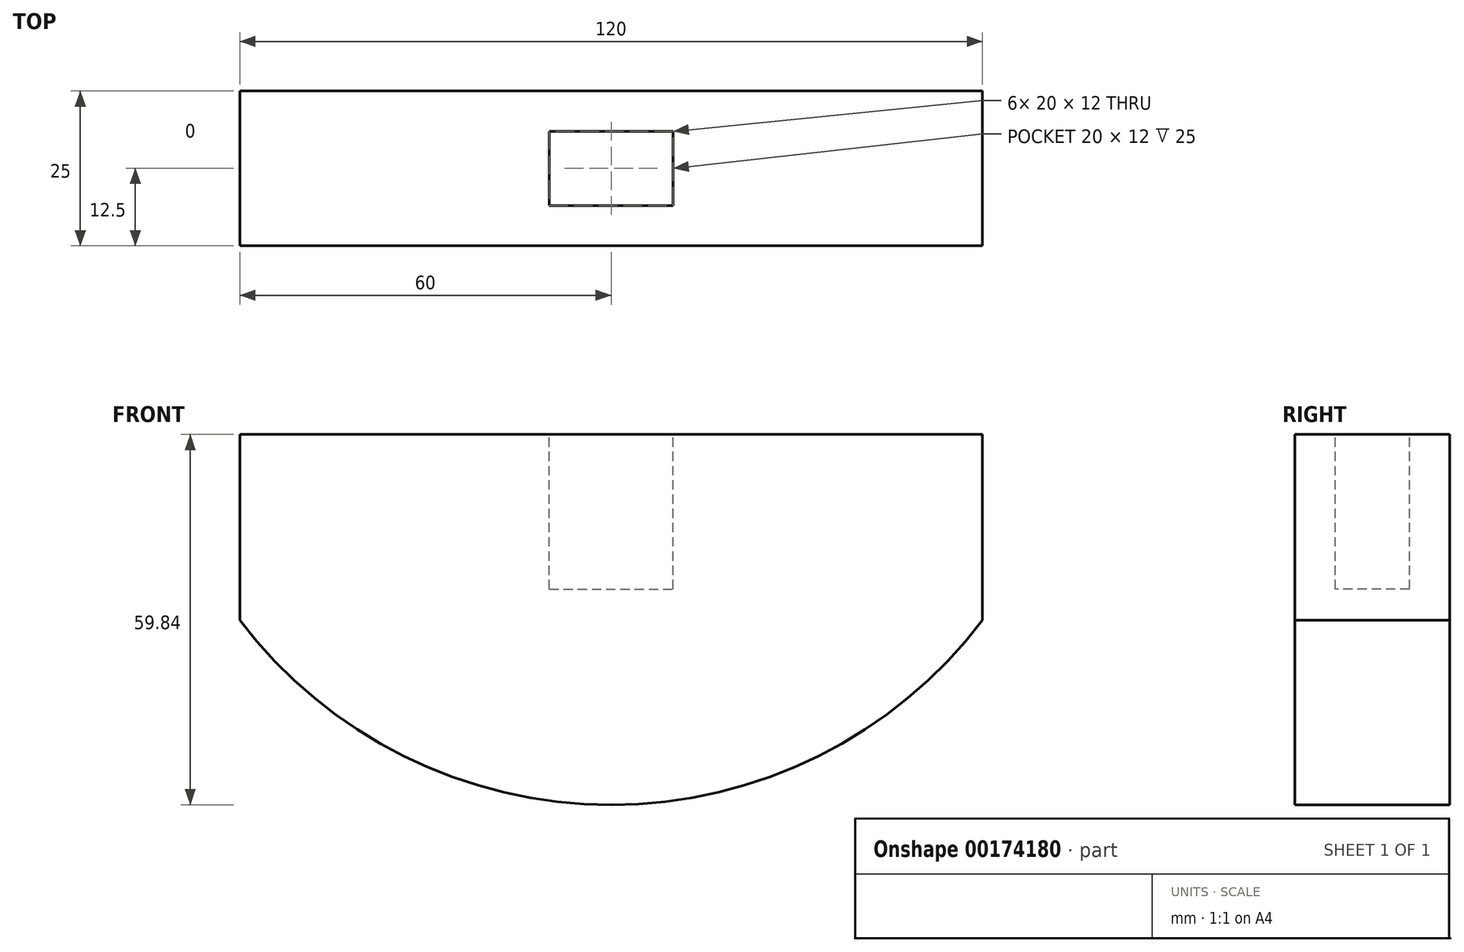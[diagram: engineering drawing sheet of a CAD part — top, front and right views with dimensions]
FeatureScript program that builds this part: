
annotation { "Feature Type Name" : "Feature", "Feature Type Description" : "" }
export const myFeature = defineFeature(function(context is Context, id is Id, definition is map)
    precondition{}
    {
        {
            var Q0;
            Q0=qCreatedBy(makeId("Front.planeOp"),FACE);
            var sketch = newSketch(context, id + "F0", { "sketchPlane" : qUnion([Q0])});
            skLineSegment(sketch, "E0.bottom", {"start": v(-60, 30) * mm, "end": v(60, 30) * mm});
            skLineSegment(sketch, "E0.left", {"start": v(-60, 30) * mm, "end": v(-60, 0) * mm});
            skLineSegment(sketch, "E0.right", {"start": v(60, 30) * mm, "end": v(60, 0) * mm});
            skArc(sketch, "E1", {"start": v(-60, 0) * mm, "mid": v(0, -29.84) * mm, "end": v(60, 0) * mm});
            skPoint(sketch, "E0.top.start.orphan", {"position": v(-60, -30) * mm});
            skPoint(sketch, "E2.orphan", {"position": v(60, -30) * mm});
            skSolve(sketch);
        }
        {
            var Q0;
            Q0=makeQuery(id+"F0.imprint","IMPRINT",FACE,{"disambiguationData":[TD([[makeQuery(id+"F0.imprint","IMPRINT",EDGE,{"derivedFrom":sQuery(id+"F0.wireOp",EDGE,"E0.bottom")}),-1.0]])]});
            extrude(context, id + "F1", {"entities" : qUnion([Q0]), "depth" : 25 * mm});
        }
        {
            var Q0;
            Q0=makeQuery(id+"F1.opExtrude","SWEPT_FACE",FACE,{"disambiguationData":[OSD([sQuery(id+"F0.wireOp",EDGE,"E0.bottom")])]});
            var sketch = newSketch(context, id + "F2", { "sketchPlane" : qUnion([Q0])});
            skLineSegment(sketch, "E3.bottom", {"start": v(-10, -6.5) * mm, "end": v(10, -6.5) * mm});
            skLineSegment(sketch, "E3.top", {"start": v(-10, -18.5) * mm, "end": v(10, -18.5) * mm});
            skLineSegment(sketch, "E3.left", {"start": v(-10, -6.5) * mm, "end": v(-10, -18.5) * mm});
            skLineSegment(sketch, "E3.right", {"start": v(10, -6.5) * mm, "end": v(10, -18.5) * mm});
            skSolve(sketch);
        }
        {
            var Q0;
            Q0=makeQuery(id+"F2.imprint","IMPRINT",FACE,{"disambiguationData":[TD([[makeQuery(id+"F2.imprint","IMPRINT",EDGE,{"derivedFrom":sQuery(id+"F2.wireOp",EDGE,"E3.bottom")}),-1.0]])]});
            extrude(context, id + "F3", {"entities" : qUnion([Q0]), "operationType" : NewBodyOperationType.REMOVE, "oppositeDirection" : true, "depth" : 25 * mm});
        }
    });
